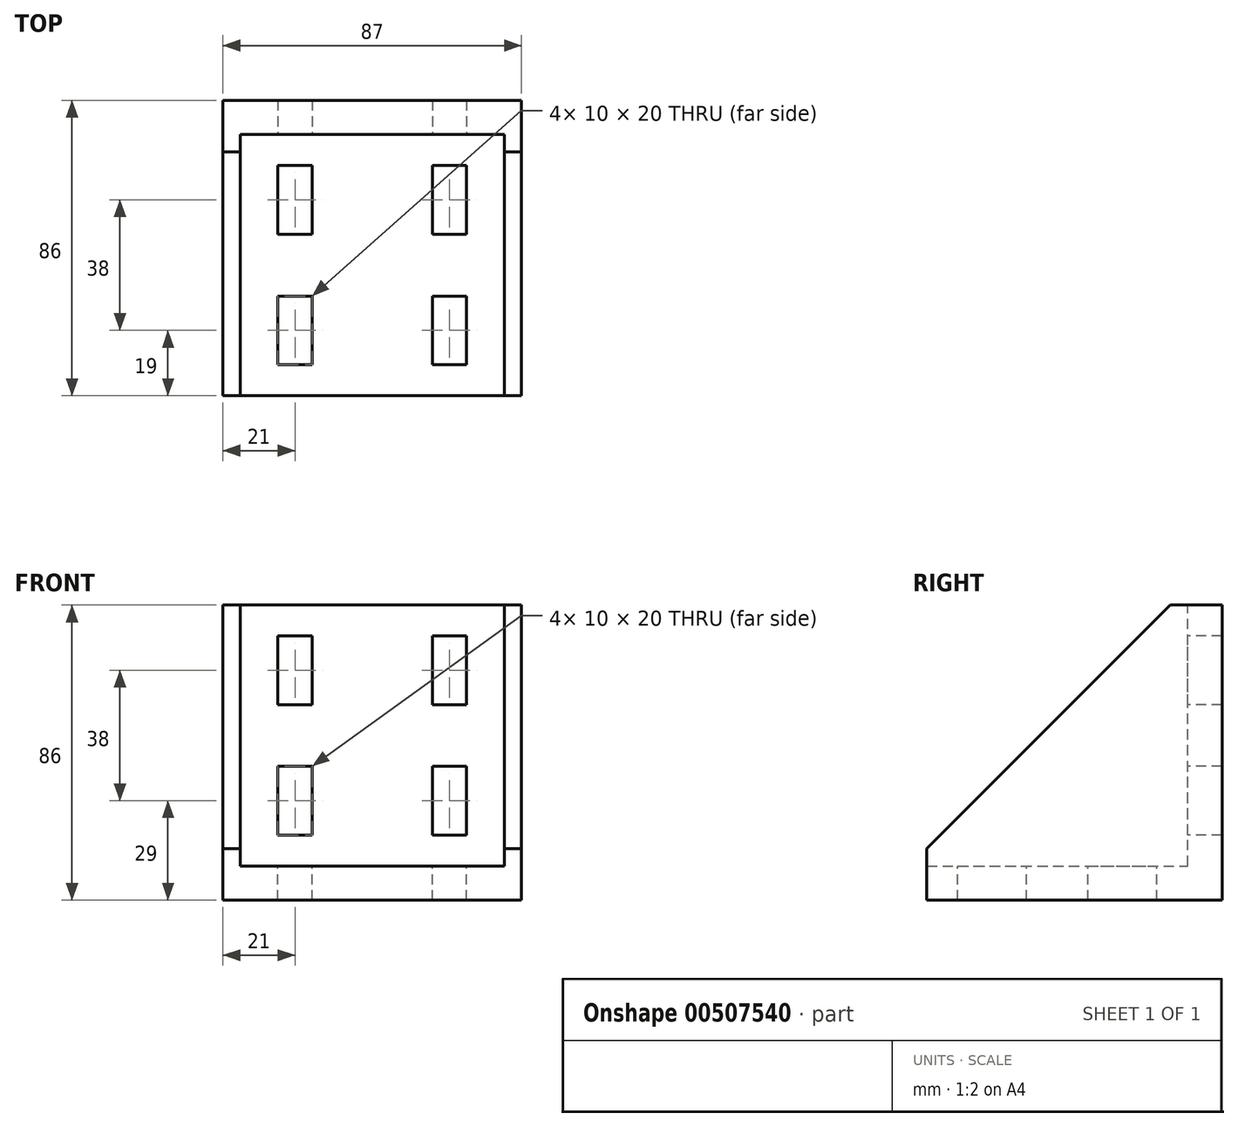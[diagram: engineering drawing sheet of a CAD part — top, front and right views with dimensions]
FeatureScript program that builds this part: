
annotation { "Feature Type Name" : "Feature", "Feature Type Description" : "" }
export const myFeature = defineFeature(function(context is Context, id is Id, definition is map)
    precondition{}
    {
        {
            var Q0;
            Q0=qCreatedBy(makeId("Front.planeOp"),FACE);
            var sketch = newSketch(context, id + "F0", { "sketchPlane" : qUnion([Q0])});
            skLineSegment(sketch, "E0.bottom", {"start": v(0, 0) * mm, "end": v(87, 0) * mm});
            skLineSegment(sketch, "E0.top", {"start": v(0, 86) * mm, "end": v(87, 86) * mm});
            skLineSegment(sketch, "E0.left", {"start": v(0, 0) * mm, "end": v(0, 86) * mm});
            skLineSegment(sketch, "E0.right", {"start": v(87, 0) * mm, "end": v(87, 86) * mm});
            skSolve(sketch);
        }
        {
            var Q0;
            Q0=qSketchRegion(id+"F0",true);
            extrude(context, id + "F1", {"entities" : qUnion([Q0]), "depth" : 10 * mm});
        }
        {
            var Q0;
            Q0=makeQuery(id+"F1.opExtrude","CAP_FACE",FACE,{"disambiguationData":[OSD([sQuery(id+"F0.wireOp",EDGE,"E0.bottom"),sQuery(id+"F0.wireOp",EDGE,"E0.top"),sQuery(id+"F0.wireOp",EDGE,"E0.left"),sQuery(id+"F0.wireOp",EDGE,"E0.right")])],"isStart":false});
            var sketch = newSketch(context, id + "F2", { "sketchPlane" : qUnion([Q0])});
            skLineSegment(sketch, "E1.bottom", {"start": v(0, 0) * mm, "end": v(87, 0) * mm});
            skLineSegment(sketch, "E1.top", {"start": v(0, 10) * mm, "end": v(87, 10) * mm});
            skLineSegment(sketch, "E1.left", {"start": v(0, 0) * mm, "end": v(0, 10) * mm});
            skLineSegment(sketch, "E1.right", {"start": v(87, 0) * mm, "end": v(87, 10) * mm});
            skSolve(sketch);
        }
        {
            var Q0;
            Q0=makeQuery(id+"F2.imprint","IMPRINT",FACE,{"disambiguationData":[TD([[makeQuery(id+"F2.imprint","IMPRINT",EDGE,{"derivedFrom":sQuery(id+"F2.wireOp",EDGE,"E1.bottom")}),1.0]])]});
            extrude(context, id + "F3", {"entities" : qUnion([Q0]), "operationType" : NewBodyOperationType.ADD, "depth" : 76 * mm});
        }
        {
            var Q0;
            Q0=makeQuery(id+"F3.boolean.opBoolean","MERGE",FACE,{"derivedFrom":[makeQuery(id+"F1.opExtrude","SWEPT_FACE",FACE,{"disambiguationData":[OSD([sQuery(id+"F0.wireOp",EDGE,"E0.right")])]}),makeQuery(id+"F3.opExtrude","SWEPT_FACE",FACE,{"disambiguationData":[OSD([sQuery(id+"F2.wireOp",EDGE,"E1.right")])]})]});
            var sketch = newSketch(context, id + "F4", { "sketchPlane" : qUnion([Q0])});
            skLineSegment(sketch, "E2", {"start": v(-86, 10) * mm, "end": v(-86, 15) * mm});
            skLineSegment(sketch, "E3", {"start": v(-86, 15) * mm, "end": v(-15, 86) * mm});
            skLineSegment(sketch, "E4", {"start": v(-15, 86) * mm, "end": v(-10, 86) * mm});
            skSolve(sketch);
        }
        {
            var Q0;
            Q0=makeQuery(id+"F4.imprint","IMPRINT",FACE,{"disambiguationData":[TD([[makeQuery(id+"F4.imprint","IMPRINT",EDGE,{"derivedFrom":sQuery(id+"F4.wireOp",EDGE,"E2")}),-1.0]])]});
            extrude(context, id + "F5", {"entities" : qUnion([Q0]), "operationType" : NewBodyOperationType.ADD, "oppositeDirection" : true, "depth" : 5 * mm});
        }
        {
            var Q0;
            Q0=makeQuery(id+"F3.boolean.opBoolean","MERGE",FACE,{"derivedFrom":[makeQuery(id+"F1.opExtrude","SWEPT_FACE",FACE,{"disambiguationData":[OSD([sQuery(id+"F0.wireOp",EDGE,"E0.left")])]}),makeQuery(id+"F3.opExtrude","SWEPT_FACE",FACE,{"disambiguationData":[OSD([sQuery(id+"F2.wireOp",EDGE,"E1.left")])]})]});
            var sketch = newSketch(context, id + "F6", { "sketchPlane" : qUnion([Q0])});
            skLineSegment(sketch, "E5", {"start": v(10, 86) * mm, "end": v(15, 86) * mm});
            skLineSegment(sketch, "E6", {"start": v(15, 86) * mm, "end": v(86, 15) * mm});
            skLineSegment(sketch, "E7", {"start": v(86, 15) * mm, "end": v(86, 10) * mm});
            skSolve(sketch);
        }
        {
            var Q0;
            Q0=makeQuery(id+"F6.imprint","IMPRINT",FACE,{"disambiguationData":[TD([[makeQuery(id+"F6.imprint","IMPRINT",EDGE,{"derivedFrom":sQuery(id+"F6.wireOp",EDGE,"E5")}),-1.0]])]});
            extrude(context, id + "F7", {"entities" : qUnion([Q0]), "operationType" : NewBodyOperationType.ADD, "oppositeDirection" : true, "depth" : 5 * mm});
        }
        {
            var Q0;
            Q0=makeQuery(id+"F1.opExtrude","CAP_FACE",FACE,{"disambiguationData":[OSD([sQuery(id+"F0.wireOp",EDGE,"E0.bottom"),sQuery(id+"F0.wireOp",EDGE,"E0.top"),sQuery(id+"F0.wireOp",EDGE,"E0.left"),sQuery(id+"F0.wireOp",EDGE,"E0.right")])],"isStart":false});
            var sketch = newSketch(context, id + "F8", { "sketchPlane" : qUnion([Q0])});
            skLineSegment(sketch, "E8.bottom", {"start": v(16, 57) * mm, "end": v(26, 57) * mm});
            skLineSegment(sketch, "E8.top", {"start": v(16, 77) * mm, "end": v(26, 77) * mm});
            skLineSegment(sketch, "E8.left", {"start": v(16, 57) * mm, "end": v(16, 77) * mm});
            skLineSegment(sketch, "E8.right", {"start": v(26, 57) * mm, "end": v(26, 77) * mm});
            skLineSegment(sketch, "E9.bottom", {"start": v(61, 57) * mm, "end": v(71, 57) * mm});
            skLineSegment(sketch, "E9.top", {"start": v(61, 77) * mm, "end": v(71, 77) * mm});
            skLineSegment(sketch, "E9.left", {"start": v(61, 57) * mm, "end": v(61, 77) * mm});
            skLineSegment(sketch, "E9.right", {"start": v(71, 57) * mm, "end": v(71, 77) * mm});
            skLineSegment(sketch, "E10.bottom", {"start": v(16, 19) * mm, "end": v(26, 19) * mm});
            skLineSegment(sketch, "E10.top", {"start": v(16, 39) * mm, "end": v(26, 39) * mm});
            skLineSegment(sketch, "E10.left", {"start": v(16, 19) * mm, "end": v(16, 39) * mm});
            skLineSegment(sketch, "E10.right", {"start": v(26, 19) * mm, "end": v(26, 39) * mm});
            skLineSegment(sketch, "E11.bottom", {"start": v(61, 19) * mm, "end": v(71, 19) * mm});
            skLineSegment(sketch, "E11.top", {"start": v(61, 39) * mm, "end": v(71, 39) * mm});
            skLineSegment(sketch, "E11.left", {"start": v(61, 19) * mm, "end": v(61, 39) * mm});
            skLineSegment(sketch, "E11.right", {"start": v(71, 19) * mm, "end": v(71, 39) * mm});
            skLineSegment(sketch, "E12", {"start": v(43.5, 86) * mm, "end": v(43.5, 48) * mm, "construction": true});
            skPoint(sketch, "E12.endSnap0", {"position": v(43.5, 10) * mm});
            skSolve(sketch);
        }
        {
            var Q0;
            Q0=makeQuery(id+"F8.imprint","IMPRINT",FACE,{"disambiguationData":[TD([[makeQuery(id+"F8.imprint","IMPRINT",EDGE,{"derivedFrom":sQuery(id+"F8.wireOp",EDGE,"E8.bottom")}),1.0]])]});
            var Q1;
            Q1=makeQuery(id+"F8.imprint","IMPRINT",FACE,{"disambiguationData":[TD([[makeQuery(id+"F8.imprint","IMPRINT",EDGE,{"derivedFrom":sQuery(id+"F8.wireOp",EDGE,"E10.bottom")}),1.0]])]});
            var Q2;
            Q2=makeQuery(id+"F8.imprint","IMPRINT",FACE,{"disambiguationData":[TD([[makeQuery(id+"F8.imprint","IMPRINT",EDGE,{"derivedFrom":sQuery(id+"F8.wireOp",EDGE,"E9.bottom")}),1.0]])]});
            var Q3;
            Q3=makeQuery(id+"F8.imprint","IMPRINT",FACE,{"disambiguationData":[TD([[makeQuery(id+"F8.imprint","IMPRINT",EDGE,{"derivedFrom":sQuery(id+"F8.wireOp",EDGE,"E11.bottom")}),1.0]])]});
            extrude(context, id + "F9", {"entities" : qUnion([Q0, Q1, Q2, Q3]), "operationType" : NewBodyOperationType.REMOVE, "oppositeDirection" : true, "depth" : 25 * mm});
        }
        {
            var Q0;
            Q0=makeQuery(id+"F3.opExtrude","SWEPT_FACE",FACE,{"disambiguationData":[OSD([sQuery(id+"F2.wireOp",EDGE,"E1.top")])]});
            var sketch = newSketch(context, id + "F10", { "sketchPlane" : qUnion([Q0])});
            skLineSegment(sketch, "E13.bottom", {"start": v(16, -39) * mm, "end": v(26, -39) * mm});
            skLineSegment(sketch, "E13.top", {"start": v(16, -19) * mm, "end": v(26, -19) * mm});
            skLineSegment(sketch, "E13.left", {"start": v(16, -39) * mm, "end": v(16, -19) * mm});
            skLineSegment(sketch, "E13.right", {"start": v(26, -39) * mm, "end": v(26, -19) * mm});
            skLineSegment(sketch, "E14.bottom", {"start": v(61, -39) * mm, "end": v(71, -39) * mm});
            skLineSegment(sketch, "E14.top", {"start": v(61, -19) * mm, "end": v(71, -19) * mm});
            skLineSegment(sketch, "E14.left", {"start": v(61, -39) * mm, "end": v(61, -19) * mm});
            skLineSegment(sketch, "E14.right", {"start": v(71, -39) * mm, "end": v(71, -19) * mm});
            skLineSegment(sketch, "E15.bottom", {"start": v(16, -77) * mm, "end": v(26, -77) * mm});
            skLineSegment(sketch, "E15.top", {"start": v(16, -57) * mm, "end": v(26, -57) * mm});
            skLineSegment(sketch, "E15.left", {"start": v(16, -77) * mm, "end": v(16, -57) * mm});
            skLineSegment(sketch, "E15.right", {"start": v(26, -77) * mm, "end": v(26, -57) * mm});
            skLineSegment(sketch, "E16.bottom", {"start": v(61, -77) * mm, "end": v(71, -77) * mm});
            skLineSegment(sketch, "E16.top", {"start": v(61, -57) * mm, "end": v(71, -57) * mm});
            skLineSegment(sketch, "E16.left", {"start": v(61, -77) * mm, "end": v(61, -57) * mm});
            skLineSegment(sketch, "E16.right", {"start": v(71, -77) * mm, "end": v(71, -57) * mm});
            skLineSegment(sketch, "E17", {"start": v(43.5, -10) * mm, "end": v(43.5, -48) * mm, "construction": true});
            skSolve(sketch);
        }
        {
            var Q0;
            Q0=makeQuery(id+"F10.imprint","IMPRINT",FACE,{"disambiguationData":[TD([[makeQuery(id+"F10.imprint","IMPRINT",EDGE,{"derivedFrom":sQuery(id+"F10.wireOp",EDGE,"E13.bottom")}),1.0]])]});
            var Q1;
            Q1=makeQuery(id+"F10.imprint","IMPRINT",FACE,{"disambiguationData":[TD([[makeQuery(id+"F10.imprint","IMPRINT",EDGE,{"derivedFrom":sQuery(id+"F10.wireOp",EDGE,"E14.bottom")}),1.0]])]});
            var Q2;
            Q2=makeQuery(id+"F10.imprint","IMPRINT",FACE,{"disambiguationData":[TD([[makeQuery(id+"F10.imprint","IMPRINT",EDGE,{"derivedFrom":sQuery(id+"F10.wireOp",EDGE,"E16.bottom")}),1.0]])]});
            var Q3;
            Q3=makeQuery(id+"F10.imprint","IMPRINT",FACE,{"disambiguationData":[TD([[makeQuery(id+"F10.imprint","IMPRINT",EDGE,{"derivedFrom":sQuery(id+"F10.wireOp",EDGE,"E15.bottom")}),1.0]])]});
            extrude(context, id + "F11", {"entities" : qUnion([Q0, Q1, Q2, Q3]), "operationType" : NewBodyOperationType.REMOVE, "oppositeDirection" : true, "depth" : 25 * mm});
        }
    });
